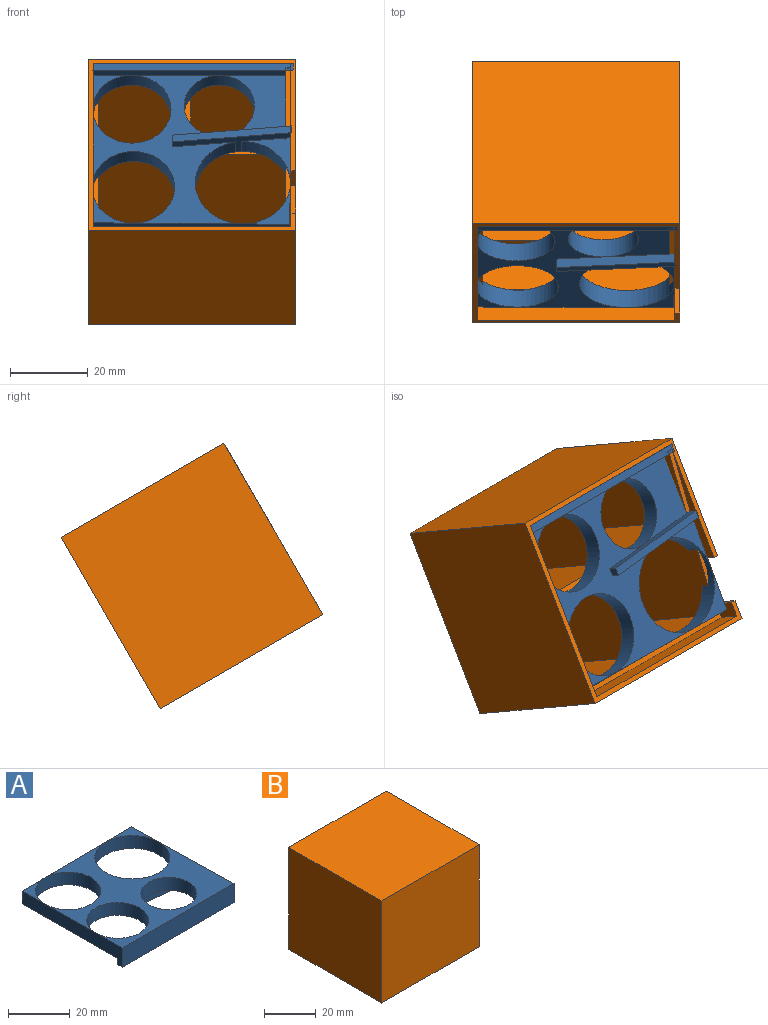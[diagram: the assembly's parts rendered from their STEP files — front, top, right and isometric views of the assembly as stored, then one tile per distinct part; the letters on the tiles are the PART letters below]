
ASSEMBLY  parts=2 mates=1
PART A: 17 faces, bbox 51.7x46.1x7.6 mm
  f0: cylinder r=12.2mm len=24.4mm, axis (0,0,-1), area 382mm2, adj f1,f10,f15
  f1: plane 51.32x44.15mm, normal (0,0,-1), area 591.9mm2, adj f0,f3,f4,f6,f7,f8,f9,f11
  f2: plane 18.91x18.06mm, normal (0,0,-1), area 195.6mm2, adj f7,f9,f11,f14
  f3: plane 50.8x5.08mm, normal (-0.01,1,0), area 258.1mm2, adj f1,f4,f9,f10
  f4: plane 45.74x7.62mm, normal (-1,-0.01,0), area 237.4mm2, adj f1,f3,f5,f10,f11,f12
  f5: plane 51.37x7.62mm, normal (0,-1,0), area 391.4mm2, adj f4,f9,f10,f12
  f6: cylinder r=10.05mm len=20.1mm, axis (0,0,-1), area 320.8mm2, adj f1,f10
  f7: cylinder r=9.05mm len=18.1mm, axis (0,0,-1), area 288.9mm2, adj f1,f2,f10
  f8: cylinder r=10.61mm len=21.21mm, axis (0,0,-1), area 338.5mm2, adj f1,f10
  f9: plane 46.15x7.62mm, normal (1,0.02,0), area 244.7mm2, adj f1,f2,f3,f5,f10,f11,f12,f14
  f10: plane 51.74x46.15mm, normal (0,0,1), area 951.5mm2, adj f0,f3,f4,f5,f6,f7,f8,f9
  f11: plane 51.34x2.54mm, normal (0,1,0), area 130.4mm2, adj f1,f2,f4,f9,f12
  f12: plane 51.38x2mm, normal (0,0,-1), area 102.7mm2, adj f4,f5,f9,f11
  f13: plane 2.54x2mm, normal (-1,0.04,0), area 5.1mm2, adj f1,f14,f15,f16
  f14: plane 30.6x2.73mm, normal (-0.09,-1,0), area 78mm2, adj f1,f2,f9,f13,f16
  f15: plane 30.48x7.62mm, normal (0.09,1,0), area 85.1mm2, adj f0,f1,f9,f10,f13,f16
  f16: plane 30.6x4.73mm, normal (0,0,-1), area 61.3mm2, adj f9,f13,f14,f15
PART B: 37 faces, bbox 53.3x50.8x48.3 mm
  f0: plane 24.5x19.42mm, normal (0,0,-1), area 475.8mm2, adj f21,f24,f34,f35
  f1: plane 24.5x24.5mm, normal (0,0,-1), area 600.2mm2, adj f5,f24,f32,f33
  f2: plane 24.5x21.96mm, normal (0,0,-1), area 538mm2, adj f5,f27,f30,f31
  f3: plane 48.26x7.62mm, normal (1,0,0), area 337.1mm2, adj f8,f14,f15,f19,f20,f26
  f4: plane 21.96x19.42mm, normal (0,0,-1), area 426.5mm2, adj f21,f27,f28,f29
  f5: plane 48.26x39.37mm, normal (0,-1,0), area 1831.4mm2, adj f1,f2,f19,f24,f27,f31,f32,f36
  f6: plane 30.48x4.23mm, normal (-1,0,0), area 64.5mm2, adj f15,f17,f22
  f7: plane 6.35x3.81mm, normal (-1,0,0), area 23.7mm2, adj f8,f15,f16,f19,f22
  f8: plane 50.8x6.35mm, normal (0,-1,0), area 322.6mm2, adj f3,f7,f15,f19
  f9: plane 50.8x48.26mm, normal (1,0,0), area 2354.8mm2, adj f11,f12,f13,f15,f16,f17,f18
  f10: plane 50.8x48.26mm, normal (-1,0,0), area 2451.6mm2, adj f11,f12,f13,f15
  f11: plane 53.34x48.26mm, normal (0,-1,0), area 2574.2mm2, adj f9,f10,f13,f15
  f12: plane 53.34x48.26mm, normal (0,1,0), area 2574.2mm2, adj f9,f10,f13,f15
  f13: plane 53.34x50.8mm, normal (0,0,1), area 2709.7mm2, adj f9,f10,f11,f12
  f14: plane 50.8x7.62mm, normal (0,1,0), area 193.5mm2, adj f3,f15,f20
  f15: plane 53.34x50.8mm, normal (0,0,-1), area 241.9mm2, adj f3,f6,f7,f8,f9,f10,f11,f12
  f16: plane 7.62x1.27mm, normal (0,-1,0), area 9.7mm2, adj f7,f9,f15,f18,f25
  f17: plane 7.62x1.27mm, normal (0,1,0), area 9.7mm2, adj f6,f9,f15,f18,f25
  f18: plane 12.7x1.27mm, normal (0,0,-1), area 16.1mm2, adj f9,f16,f17,f25
  f19: plane 50.8x1.27mm, normal (0,0,-1), area 64.5mm2, adj f3,f5,f7,f8,f22,f26
  f20: plane 50.8x7.62mm, normal (-0.15,0,-0.99), area 65.2mm2, adj f3,f14,f15,f21,f23
  f21: plane 49.53x45.53mm, normal (0,1,0), area 1954.1mm2, adj f0,f4,f20,f24,f26,f27,f28,f35
  f22: plane 45.72x6.35mm, normal (0,0.14,-0.99), area 58.6mm2, adj f6,f7,f19,f23,f24,f25
  f23: plane 1.27x0.19mm, normal (0,-1,0), area 0.1mm2, adj f20,f22,f24
  f24: plane 45.72x45.72mm, normal (-1,0,0), area 1876.6mm2, adj f0,f1,f5,f21,f22,f23,f33,f34
  f25: plane 12.7x3.39mm, normal (1,0,0), area 31.8mm2, adj f16,f17,f18,f22
  f26: plane 45.72x1.27mm, normal (0,-0.03,-1), area 58.1mm2, adj f3,f19,f21,f27
  f27: plane 45.72x39.37mm, normal (1,0,0), area 1702.4mm2, adj f2,f4,f5,f21,f26,f29,f30,f36
  f28: plane 38.1x19.42mm, normal (-1,0,0), area 739.9mm2, adj f4,f21,f29,f36
  f29: plane 38.1x21.96mm, normal (0,-1,0), area 836.7mm2, adj f4,f27,f28,f36
  f30: plane 38.1x21.96mm, normal (0,1,0), area 836.7mm2, adj f2,f27,f31,f36
  f31: plane 38.1x24.5mm, normal (-1,0,0), area 933.4mm2, adj f2,f5,f30,f36
  f32: plane 38.1x24.5mm, normal (1,0,0), area 933.4mm2, adj f1,f5,f33,f36
  f33: plane 38.1x24.5mm, normal (0,1,0), area 933.4mm2, adj f1,f24,f32,f36
  f34: plane 38.1x24.5mm, normal (0,-1,0), area 933.4mm2, adj f0,f24,f35,f36
  f35: plane 38.1x19.42mm, normal (1,0,0), area 739.9mm2, adj f0,f21,f34,f36
  f36: plane 48.26x45.72mm, normal (0,0,-1), area 165.9mm2, adj f5,f21,f24,f27,f28,f29,f30,f31
PLACE A rot(axis=(-1,0,0),120deg) t=(0,-42.86,-14.67)mm
PLACE B rot(axis=(-1,0,0),120deg) t=(77.1,-0.27,-27.27)mm
MATE fastened B.f36 <-> A.f10  axis (0,0.87,-0.5) through (58.24,-24.39,7.16)mm
